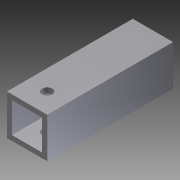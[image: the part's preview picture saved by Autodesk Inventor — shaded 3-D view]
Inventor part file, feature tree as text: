
AUTODESK INVENTOR PART (.ipt)
format: ipt  version: 2012 (Build 160160000, 160)  size: 92,672 bytes
history: native  units: in
note: dims shown in document units (in); Inventor stores cm internally (conversion verified against a paired STEP export)
features: extrude x2, sketch x2
ambient origin geometry x8: Origin, YZ Plane, XZ Plane, XY Plane, X Axis, Y Axis, Z Axis, Center Point
bodies: Solid1 (feature_tree)
feature tree (4):
  extrude  "Extrusion1"  Depth=1.0in
  extrude  "Extrusion3"  Depth=0.5in
  sketch  "Sketch1"  dims[d0=1.0in d1=1.0in]
  sketch  "Sketch3"  dims[d2=0.5in d3=0.5in d4=0.125in d5=0.125in d6=0.125in d7=0.125in d8=3.125in d9=0.0in d13=2.625in d14=0.5in d15=0.25in d16=1.0in d17=0.0in]
